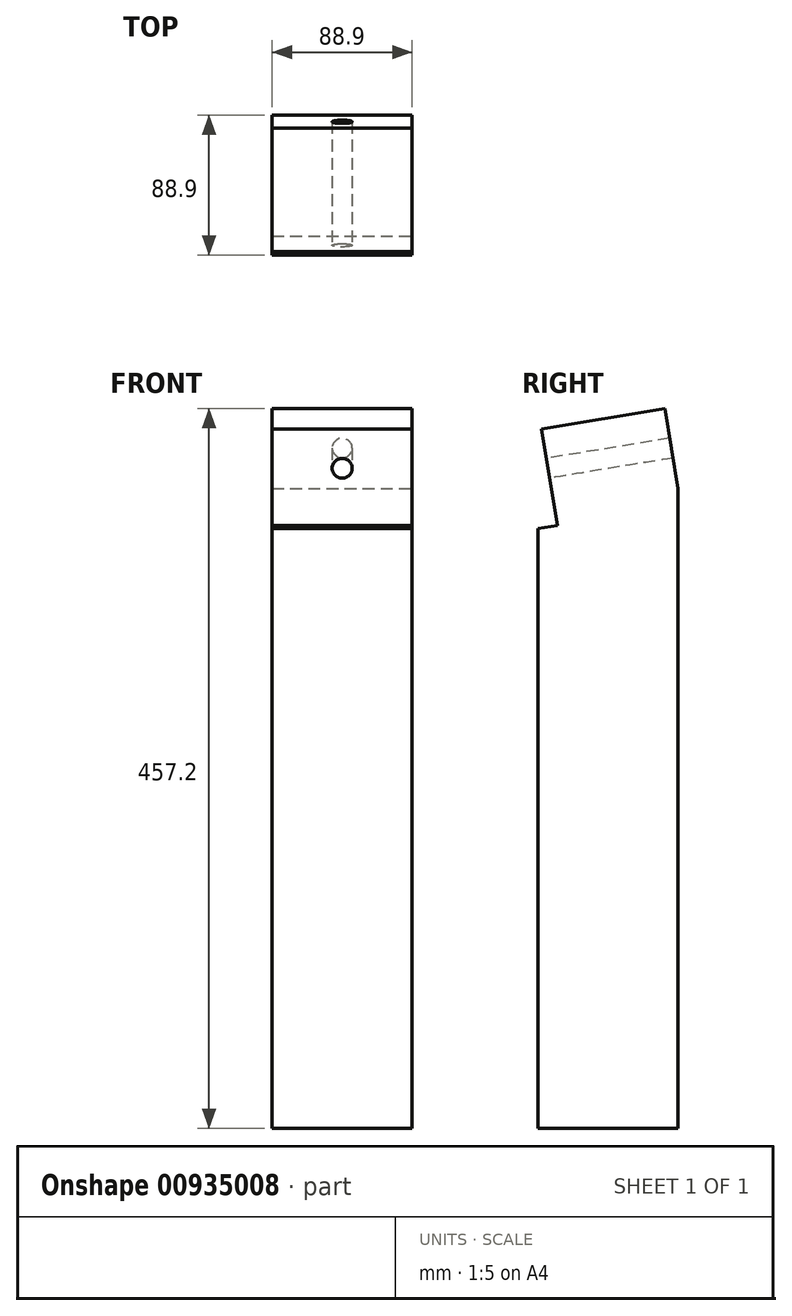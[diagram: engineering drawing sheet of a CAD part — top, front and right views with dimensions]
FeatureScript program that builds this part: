
annotation { "Feature Type Name" : "Feature", "Feature Type Description" : "" }
export const myFeature = defineFeature(function(context is Context, id is Id, definition is map)
    precondition{}
    {
        {
            var Q0;
            Q0=qCreatedBy(makeId("Front.planeOp"),FACE);
            var sketch = newSketch(context, id + "F0", { "sketchPlane" : qUnion([Q0])});
            skLineSegment(sketch, "E0.bottom", {"start": v(44.45, -228.6) * mm, "end": v(-44.45, -228.6) * mm});
            skLineSegment(sketch, "E0.top", {"start": v(44.45, 228.6) * mm, "end": v(-44.45, 228.6) * mm});
            skLineSegment(sketch, "E0.left", {"start": v(44.45, -228.6) * mm, "end": v(44.45, 228.6) * mm});
            skLineSegment(sketch, "E0.right", {"start": v(-44.45, -228.6) * mm, "end": v(-44.45, 228.6) * mm});
            skPoint(sketch, "E0.middle", {"position": v(0, 0) * mm});
            skSolve(sketch);
        }
        {
            var Q0;
            Q0 = qSketchRegion(id + "F0", true);
            extrude(context, id + "F1", {"entities" : qUnion([Q0]), "depth" : 88.9 * mm, "offsetDistance" : 25.4 * mm, "symmetric" : true});
        }
        {
            var Q0;
            Q0=qCreatedBy(makeId("Right.planeOp"),FACE);
            var sketch = newSketch(context, id + "F2", { "sketchPlane" : qUnion([Q0])});
            skLineSegment(sketch, "E1", {"start": v(44.45, 228.6) * mm, "end": v(36.13, 228.6) * mm});
            skLineSegment(sketch, "E2", {"start": v(36.13, 228.6) * mm, "end": v(44.45, 177.8) * mm});
            skLineSegment(sketch, "E3", {"start": v(44.45, 177.8) * mm, "end": v(44.45, 228.6) * mm});
            skLineSegment(sketch, "E4", {"start": v(-44.45, 228.6) * mm, "end": v(-32.3, 154.4) * mm});
            skLineSegment(sketch, "E5", {"start": v(-32.3, 154.4) * mm, "end": v(-44.45, 152.4) * mm});
            skLineSegment(sketch, "E6", {"start": v(-44.45, 152.4) * mm, "end": v(-44.45, 228.6) * mm});
            skLineSegment(sketch, "E7", {"start": v(-44.45, 228.6) * mm, "end": v(-42.35, 215.75) * mm});
            skLineSegment(sketch, "E8", {"start": v(36.13, 228.6) * mm, "end": v(-42.35, 215.75) * mm});
            skLineSegment(sketch, "E9", {"start": v(-44.45, 228.6) * mm, "end": v(34.03, 241.45) * mm});
            skLineSegment(sketch, "E10", {"start": v(34.03, 241.45) * mm, "end": v(36.13, 228.6) * mm});
            skSolve(sketch);
        }
        {
            var Q0;
            Q0 = qSketchRegion(id + "F2", true);
            extrude(context, id + "F3", {"entities" : qUnion([Q0]), "operationType" : NewBodyOperationType.REMOVE, "oppositeDirection" : true, "depth" : 254 * mm, "offsetDistance" : 25.4 * mm, "symmetric" : true});
        }
        {
            var Q0;
            Q0=makeQuery(id+"F3.boolean.opBoolean","COPY",FACE,{"derivedFrom":makeQuery(id+"F3.opExtrude","SWEPT_FACE",FACE,{"disambiguationData":[OSD([sQuery(id+"F2.wireOp",EDGE,"E4")])]})});
            var sketch = newSketch(context, id + "F4", { "sketchPlane" : qUnion([Q0])});
            skCircle(sketch, "E11", {"center": v(0, 194.36) * mm, "radius": 6.35 * mm});
            skSolve(sketch);
        }
        {
            var Q0;
            Q0 = qSketchRegion(id + "F4", true);
            extrude(context, id + "F5", {"entities" : qUnion([Q0]), "operationType" : NewBodyOperationType.REMOVE, "oppositeDirection" : true, "depth" : 254 * mm, "offsetDistance" : 25.4 * mm, "symmetric" : true});
        }
    });
